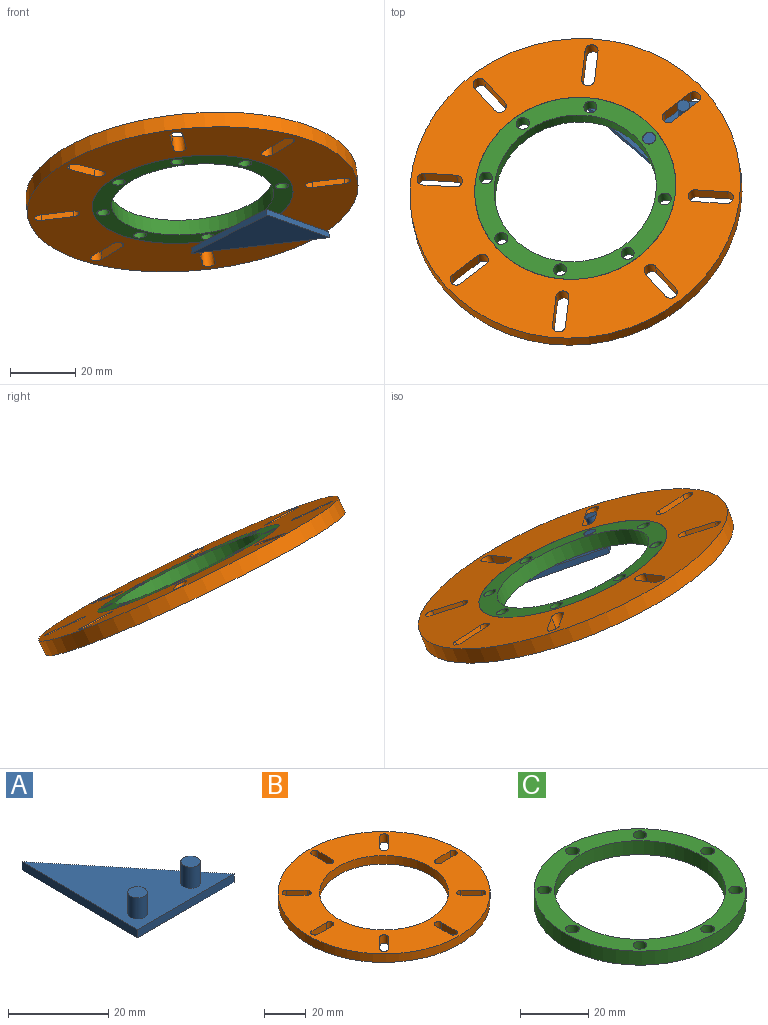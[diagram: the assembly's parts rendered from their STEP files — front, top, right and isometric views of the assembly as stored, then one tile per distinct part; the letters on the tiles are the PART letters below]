
ASSEMBLY  parts=3 mates=3
PART A: 9 faces, bbox 27.3x33x7.2 mm
  f0: plane 32.97x2mm, normal (-1,0.01,0), area 65.9mm2, adj f1,f2,f3,f4
  f1: plane 27.33x2mm, normal (0,-1,0), area 54.7mm2, adj f0,f2,f3,f4
  f2: plane 32.97x26.98mm, normal (0.77,0.63,0), area 85.2mm2, adj f0,f1,f3,f4
  f3: plane 32.97x27.33mm, normal (0,0,1), area 426.6mm2, adj f0,f1,f2,f5,f7
  f4: plane 32.97x27.33mm, normal (0,0,-1), area 450.5mm2, adj f0,f1,f2
  f5: cylinder r=1.95mm len=5.2mm, axis (0,0,-1), area 63.7mm2, adj f3,f6
  f6: plane 3.9x3.9mm, normal (0,0,1), area 11.9mm2, adj f5
  f7: cylinder r=1.95mm len=5.2mm, axis (0,0,-1), area 63.7mm2, adj f3,f8
  f8: plane 3.9x3.9mm, normal (0,0,1), area 11.9mm2, adj f7
PART B: 36 faces, bbox 102x102x5 mm
  f0: cylinder r=2mm len=5mm, axis (0,0,-1), area 31.4mm2, adj f1,f24,f34,f35
  f1: plane 10x5mm, normal (-1,0,0), area 50mm2, adj f0,f2,f34,f35
  f2: cylinder r=2mm len=5mm, axis (0,0,-1), area 31.4mm2, adj f1,f24,f34,f35
  f3: plane 7.07x7.07mm, normal (0.71,-0.71,0), area 50mm2, adj f4,f26,f34,f35
  f4: cylinder r=2mm len=5mm, axis (0,0,-1), area 31.4mm2, adj f3,f5,f34,f35
  f5: plane 7.07x7.07mm, normal (-0.71,0.71,0), area 50mm2, adj f4,f26,f34,f35
  f6: plane 10x5mm, normal (0,-1,0), area 50mm2, adj f7,f27,f34,f35
  f7: cylinder r=2mm len=5mm, axis (0,0,-1), area 31.4mm2, adj f6,f8,f34,f35
  f8: plane 10x5mm, normal (0,1,0), area 50mm2, adj f7,f27,f34,f35
  f9: plane 7.07x7.07mm, normal (-0.71,-0.71,0), area 50mm2, adj f10,f28,f34,f35
  f10: cylinder r=2mm len=5mm, axis (0,0,-1), area 31.4mm2, adj f9,f11,f34,f35
  f11: plane 7.07x7.07mm, normal (0.71,0.71,0), area 50mm2, adj f10,f28,f34,f35
  f12: plane 10x5mm, normal (-1,0,0), area 50mm2, adj f13,f29,f34,f35
  f13: cylinder r=2mm len=5mm, axis (0,0,-1), area 31.4mm2, adj f12,f14,f34,f35
  f14: plane 10x5mm, normal (1,0,0), area 50mm2, adj f13,f29,f34,f35
  f15: plane 7.07x7.07mm, normal (-0.71,0.71,0), area 50mm2, adj f16,f30,f34,f35
  f16: cylinder r=2mm len=5mm, axis (0,0,-1), area 31.4mm2, adj f15,f17,f34,f35
  f17: plane 7.07x7.07mm, normal (0.71,-0.71,0), area 50mm2, adj f16,f30,f34,f35
  f18: plane 10x5mm, normal (0,1,0), area 50mm2, adj f19,f31,f34,f35
  f19: cylinder r=2mm len=5mm, axis (0,0,-1), area 31.4mm2, adj f18,f20,f34,f35
  f20: plane 10x5mm, normal (0,-1,0), area 50mm2, adj f19,f31,f34,f35
  f21: plane 7.07x7.07mm, normal (0.71,0.71,0), area 50mm2, adj f22,f32,f34,f35
  f22: cylinder r=2mm len=5mm, axis (0,0,-1), area 31.4mm2, adj f21,f23,f34,f35
  f23: plane 7.07x7.07mm, normal (-0.71,-0.71,0), area 50mm2, adj f22,f32,f34,f35
  f24: plane 10x5mm, normal (1,0,0), area 50mm2, adj f0,f2,f34,f35
  f25: cylinder r=31mm len=62mm, axis (0,0,-1), area 973.9mm2, adj f34,f35
  f26: cylinder r=2mm len=5mm, axis (0,0,-1), area 31.4mm2, adj f3,f5,f34,f35
  f27: cylinder r=2mm len=5mm, axis (0,0,-1), area 31.4mm2, adj f6,f8,f34,f35
  f28: cylinder r=2mm len=5mm, axis (0,0,-1), area 31.4mm2, adj f9,f11,f34,f35
  f29: cylinder r=2mm len=5mm, axis (0,0,-1), area 31.4mm2, adj f12,f14,f34,f35
  f30: cylinder r=2mm len=5mm, axis (0,0,-1), area 31.4mm2, adj f15,f17,f34,f35
  f31: cylinder r=2mm len=5mm, axis (0,0,-1), area 31.4mm2, adj f18,f20,f34,f35
  f32: cylinder r=2mm len=5mm, axis (0,0,-1), area 31.4mm2, adj f21,f23,f34,f35
  f33: cylinder r=51mm len=102mm, axis (0,0,-1), area 1602.2mm2, adj f34,f35
  f34: plane 102x102mm, normal (0,0,1), area 4731.7mm2, adj f0,f1,f2,f3,f4,f5,f6,f7
  f35: plane 102x102mm, normal (0,0,-1), area 4731.7mm2, adj f0,f1,f2,f3,f4,f5,f6,f7
PART C: 12 faces, bbox 62x62x5 mm
  f0: cylinder r=2mm len=5mm, axis (0,0,-1), area 62.8mm2, adj f10,f11
  f1: cylinder r=2mm len=5mm, axis (0,0,-1), area 62.8mm2, adj f10,f11
  f2: cylinder r=2mm len=5mm, axis (0,0,-1), area 62.8mm2, adj f10,f11
  f3: cylinder r=2mm len=5mm, axis (0,0,-1), area 62.8mm2, adj f10,f11
  f4: cylinder r=2mm len=5mm, axis (0,0,-1), area 62.8mm2, adj f10,f11
  f5: cylinder r=2mm len=5mm, axis (0,0,-1), area 62.8mm2, adj f10,f11
  f6: cylinder r=2mm len=5mm, axis (0,0,-1), area 62.8mm2, adj f10,f11
  f7: cylinder r=2mm len=5mm, axis (0,0,-1), area 62.8mm2, adj f10,f11
  f8: cylinder r=25mm len=50mm, axis (0,0,-1), area 785.4mm2, adj f10,f11
  f9: cylinder r=31mm len=62mm, axis (0,0,-1), area 973.9mm2, adj f10,f11
  f10: plane 62x62mm, normal (0,0,1), area 955mm2, adj f0,f1,f2,f3,f4,f5,f6,f7
  f11: plane 62x62mm, normal (0,0,-1), area 955mm2, adj f0,f1,f2,f3,f4,f5,f6,f7
PLACE A rot(axis=(-0.49,0.11,0.86),52.8deg) t=(17.4,440.06,1002.23)mm
PLACE B rot(axis=(-0.27,0.17,0.95),88.1deg) t=(-5.49,430.66,1007.06)mm
PLACE C rot(axis=(-0.59,0.08,0.81),44.5deg) t=(-5.49,430.66,1007.06)mm
MATE revolute A.f7 <-> C.f5  axis (-0.08,0.43,0.9) through (16.8,448.22,1006.29)mm
MATE pin_slot A.f5 <-> B.f32  axis (-0.08,0.43,0.9) through (27.3,458.23,1002.48)mm
MATE revolute B.f25 <-> C.f9  axis (0.08,-0.43,-0.9) through (-5.7,431.73,1009.31)mm
